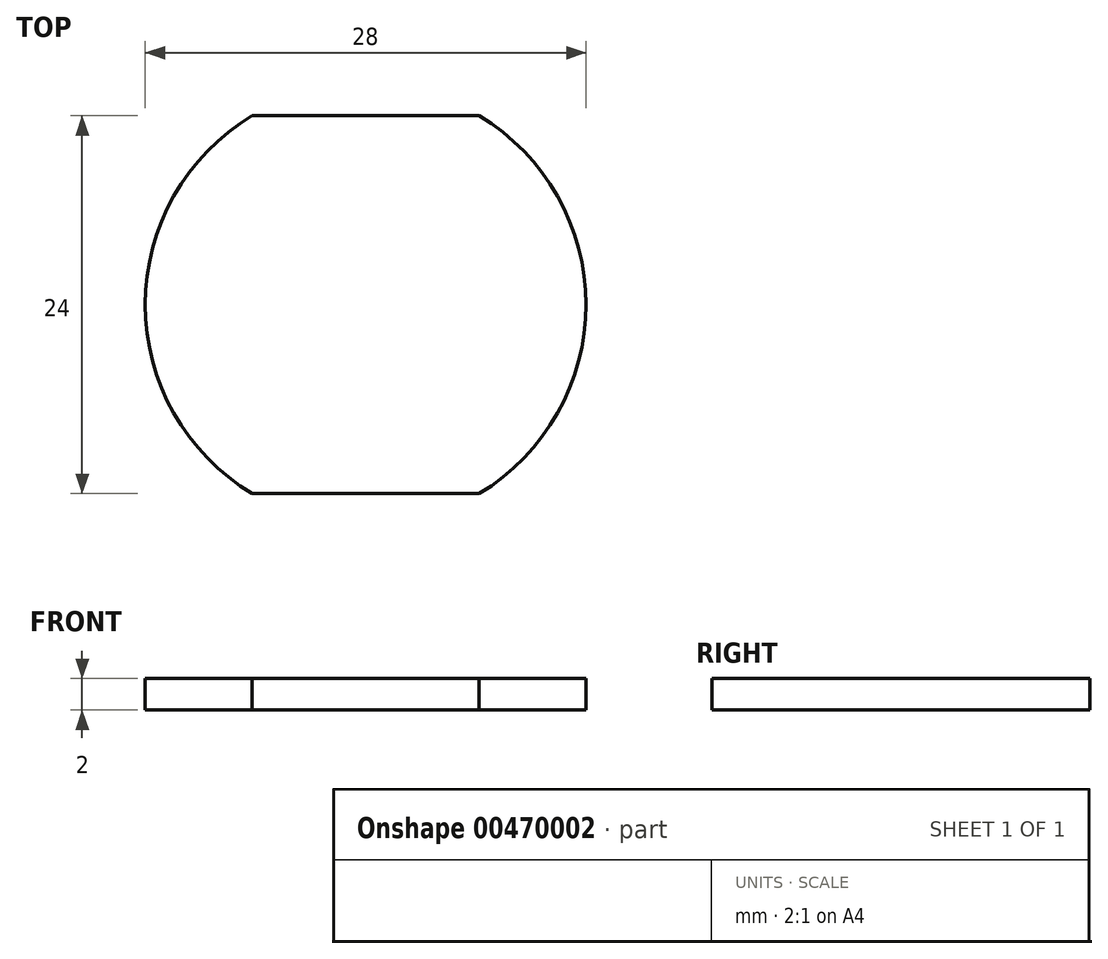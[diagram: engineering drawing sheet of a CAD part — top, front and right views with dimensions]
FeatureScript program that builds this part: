
annotation { "Feature Type Name" : "Feature", "Feature Type Description" : "" }
export const myFeature = defineFeature(function(context is Context, id is Id, definition is map)
    precondition{}
    {
        {
            var Q0;
            Q0=qCreatedBy(makeId("Top.planeOp"),FACE);
            var sketch = newSketch(context, id + "F0", { "sketchPlane" : qUnion([Q0])});
            skCircle(sketch, "E0", {"center": v(0, 0) * mm, "radius": 14 * mm});
            skLineSegment(sketch, "E1", {"start": v(0, 14) * mm, "end": v(0, 12) * mm});
            skLineSegment(sketch, "E2", {"start": v(7.21, 12) * mm, "end": v(-7.21, 12) * mm});
            skLineSegment(sketch, "E3.1.0", {"start": v(-7.21, -12) * mm, "end": v(7.21, -12) * mm});
            skSolve(sketch);
        }
        {
            var Q0;
            {var subQ4=sQuery(id+"F0.wireOp",EDGE,"E3.1.0");Q0=makeQuery(id+"F0.imprint","IMPRINT",FACE,{"disambiguationData":[TD([[makeQuery(id+"F0.imprint","IMPRINT",EDGE,{"derivedFrom":subQ4}),1.0]])]});}
            extrude(context, id + "F1", {"entities" : qUnion([Q0]), "depth" : 2 * mm, "offsetDistance" : 25 * mm});
        }
    });
